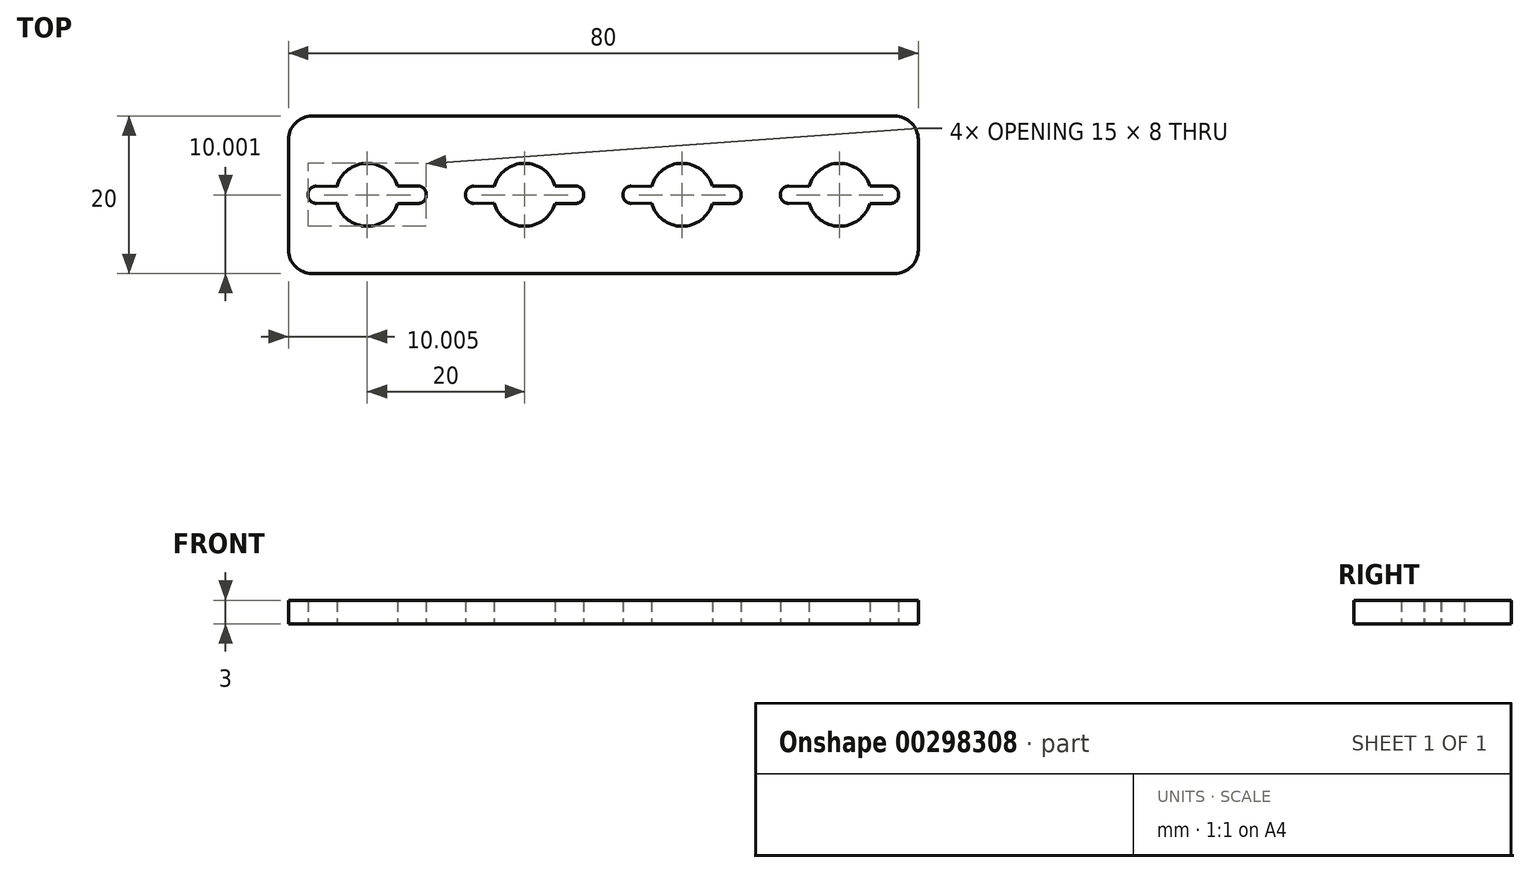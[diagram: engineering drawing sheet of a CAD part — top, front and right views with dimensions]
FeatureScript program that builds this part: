
annotation { "Feature Type Name" : "Feature", "Feature Type Description" : "" }
export const myFeature = defineFeature(function(context is Context, id is Id, definition is map)
    precondition{}
    {
        {
            var Q0;
            Q0=qCreatedBy(makeId("Top.planeOp"),FACE);
            var sketch = newSketch(context, id + "F0", { "sketchPlane" : qUnion([Q0])});
            skLineSegment(sketch, "E0.bottom", {"start": v(-30.97, -3.38) * mm, "end": v(43.03, -3.38) * mm});
            skLineSegment(sketch, "E0.top", {"start": v(-30.97, -23.38) * mm, "end": v(43.03, -23.38) * mm});
            skLineSegment(sketch, "E0.left", {"start": v(-33.97, -6.38) * mm, "end": v(-33.97, -20.38) * mm});
            skLineSegment(sketch, "E0.right", {"start": v(46.03, -6.38) * mm, "end": v(46.03, -20.38) * mm});
            skPoint(sketch, "E1.visualSharp", {"position": v(-33.97, -23.38) * mm});
            skArc(sketch, "E1.filletArc", {"start": v(-33.97, -20.38) * mm, "mid": v(-33.09, -22.5) * mm, "end": v(-30.97, -23.38) * mm});
            skPoint(sketch, "E2.visualSharp", {"position": v(-33.97, -3.38) * mm});
            skArc(sketch, "E2.filletArc", {"start": v(-30.97, -3.38) * mm, "mid": v(-33.09, -4.26) * mm, "end": v(-33.97, -6.38) * mm});
            skPoint(sketch, "E3.visualSharp", {"position": v(46.03, -3.38) * mm});
            skArc(sketch, "E3.filletArc", {"start": v(46.03, -6.38) * mm, "mid": v(45.16, -4.26) * mm, "end": v(43.03, -3.38) * mm});
            skPoint(sketch, "E4.visualSharp", {"position": v(46.03, -23.38) * mm});
            skArc(sketch, "E4.filletArc", {"start": v(43.03, -23.38) * mm, "mid": v(45.16, -22.5) * mm, "end": v(46.03, -20.38) * mm});
            skArc(sketch, "E5", {"start": v(-20.12, -12.28) * mm, "mid": v(-23.99, -9.38) * mm, "end": v(-27.82, -12.32) * mm});
            skLineSegment(sketch, "E6", {"start": v(-20.12, -12.28) * mm, "end": v(-17.47, -12.28) * mm});
            skLineSegment(sketch, "E7", {"start": v(-16.47, -13.28) * mm, "end": v(-16.47, -13.48) * mm});
            skLineSegment(sketch, "E8", {"start": v(-27.82, -12.32) * mm, "end": v(-30.45, -12.29) * mm});
            skLineSegment(sketch, "E9.MirrorCS", {"start": v(-20.12, -14.48) * mm, "end": v(-17.47, -14.48) * mm});
            skArc(sketch, "E10.MirrorCS", {"start": v(-20.12, -14.48) * mm, "mid": v(-23.99, -17.38) * mm, "end": v(-27.82, -14.44) * mm});
            skLineSegment(sketch, "E11.MirrorCS", {"start": v(-27.82, -14.44) * mm, "end": v(-30.45, -14.47) * mm});
            skLineSegment(sketch, "E12", {"start": v(-31.47, -13.29) * mm, "end": v(-31.47, -13.47) * mm});
            skPoint(sketch, "E13.visualSharp", {"position": v(-16.47, -12.28) * mm});
            skArc(sketch, "E13.filletArc", {"start": v(-16.47, -13.28) * mm, "mid": v(-16.76, -12.57) * mm, "end": v(-17.47, -12.28) * mm});
            skPoint(sketch, "E14.visualSharp", {"position": v(-16.47, -14.48) * mm});
            skArc(sketch, "E14.filletArc", {"start": v(-17.47, -14.48) * mm, "mid": v(-16.76, -14.19) * mm, "end": v(-16.47, -13.48) * mm});
            skPoint(sketch, "E15.visualSharp", {"position": v(-31.47, -12.28) * mm});
            skArc(sketch, "E15.filletArc", {"start": v(-30.45, -12.29) * mm, "mid": v(-31.17, -12.58) * mm, "end": v(-31.47, -13.29) * mm});
            skPoint(sketch, "E16.visualSharp", {"position": v(-31.47, -14.48) * mm});
            skArc(sketch, "E16.filletArc", {"start": v(-31.47, -13.47) * mm, "mid": v(-31.17, -14.18) * mm, "end": v(-30.45, -14.47) * mm});
            skLineSegment(sketch, "E17.1.0.0", {"start": v(-7.82, -12.32) * mm, "end": v(-10.45, -12.29) * mm});
            skPoint(sketch, "E17.1.0.1", {"position": v(3.53, -12.28) * mm});
            skLineSegment(sketch, "E17.1.0.2", {"start": v(-0.12, -12.28) * mm, "end": v(2.53, -12.28) * mm});
            skLineSegment(sketch, "E17.1.0.3", {"start": v(-0.12, -14.48) * mm, "end": v(2.53, -14.48) * mm});
            skPoint(sketch, "E17.1.0.4", {"position": v(3.53, -14.48) * mm});
            skArc(sketch, "E17.1.0.5", {"start": v(-0.12, -12.28) * mm, "mid": v(-3.99, -9.38) * mm, "end": v(-7.82, -12.32) * mm});
            skPoint(sketch, "E17.1.0.6", {"position": v(-11.47, -12.28) * mm});
            skPoint(sketch, "E17.1.0.7", {"position": v(-11.47, -14.48) * mm});
            skLineSegment(sketch, "E17.1.0.8", {"start": v(-7.82, -14.44) * mm, "end": v(-10.45, -14.47) * mm});
            skArc(sketch, "E17.1.0.9", {"start": v(-0.12, -14.48) * mm, "mid": v(-3.99, -17.38) * mm, "end": v(-7.82, -14.44) * mm});
            skArc(sketch, "E17.1.0.10", {"start": v(3.53, -13.28) * mm, "mid": v(3.24, -12.57) * mm, "end": v(2.53, -12.28) * mm});
            skArc(sketch, "E17.1.0.11", {"start": v(-10.45, -12.29) * mm, "mid": v(-11.17, -12.58) * mm, "end": v(-11.47, -13.29) * mm});
            skArc(sketch, "E17.1.0.12", {"start": v(2.53, -14.48) * mm, "mid": v(3.24, -14.19) * mm, "end": v(3.53, -13.48) * mm});
            skArc(sketch, "E17.1.0.13", {"start": v(-11.47, -13.47) * mm, "mid": v(-11.17, -14.18) * mm, "end": v(-10.45, -14.47) * mm});
            skLineSegment(sketch, "E17.1.0.14", {"start": v(3.53, -13.28) * mm, "end": v(3.53, -13.48) * mm});
            skLineSegment(sketch, "E17.1.0.15", {"start": v(-11.47, -13.29) * mm, "end": v(-11.47, -13.47) * mm});
            skLineSegment(sketch, "E17.2.0.0", {"start": v(12.18, -12.32) * mm, "end": v(9.55, -12.29) * mm});
            skPoint(sketch, "E17.2.0.1", {"position": v(23.53, -12.28) * mm});
            skLineSegment(sketch, "E17.2.0.2", {"start": v(19.88, -12.28) * mm, "end": v(22.53, -12.28) * mm});
            skLineSegment(sketch, "E17.2.0.3", {"start": v(19.88, -14.48) * mm, "end": v(22.53, -14.48) * mm});
            skPoint(sketch, "E17.2.0.4", {"position": v(23.53, -14.48) * mm});
            skArc(sketch, "E17.2.0.5", {"start": v(19.88, -12.28) * mm, "mid": v(16.01, -9.38) * mm, "end": v(12.18, -12.32) * mm});
            skPoint(sketch, "E17.2.0.6", {"position": v(8.53, -12.28) * mm});
            skPoint(sketch, "E17.2.0.7", {"position": v(8.53, -14.48) * mm});
            skLineSegment(sketch, "E17.2.0.8", {"start": v(12.18, -14.44) * mm, "end": v(9.55, -14.47) * mm});
            skArc(sketch, "E17.2.0.9", {"start": v(19.88, -14.48) * mm, "mid": v(16.01, -17.38) * mm, "end": v(12.18, -14.44) * mm});
            skArc(sketch, "E17.2.0.10", {"start": v(23.53, -13.28) * mm, "mid": v(23.24, -12.57) * mm, "end": v(22.53, -12.28) * mm});
            skArc(sketch, "E17.2.0.11", {"start": v(9.55, -12.29) * mm, "mid": v(8.83, -12.58) * mm, "end": v(8.53, -13.29) * mm});
            skArc(sketch, "E17.2.0.12", {"start": v(22.53, -14.48) * mm, "mid": v(23.24, -14.19) * mm, "end": v(23.53, -13.48) * mm});
            skArc(sketch, "E17.2.0.13", {"start": v(8.53, -13.47) * mm, "mid": v(8.83, -14.18) * mm, "end": v(9.55, -14.47) * mm});
            skLineSegment(sketch, "E17.2.0.14", {"start": v(23.53, -13.28) * mm, "end": v(23.53, -13.48) * mm});
            skLineSegment(sketch, "E17.2.0.15", {"start": v(8.53, -13.29) * mm, "end": v(8.53, -13.47) * mm});
            skLineSegment(sketch, "E17.3.0.0", {"start": v(32.18, -12.32) * mm, "end": v(29.55, -12.29) * mm});
            skPoint(sketch, "E17.3.0.1", {"position": v(43.53, -12.28) * mm});
            skLineSegment(sketch, "E17.3.0.2", {"start": v(39.88, -12.28) * mm, "end": v(42.53, -12.28) * mm});
            skLineSegment(sketch, "E17.3.0.3", {"start": v(39.88, -14.48) * mm, "end": v(42.53, -14.48) * mm});
            skPoint(sketch, "E17.3.0.4", {"position": v(43.53, -14.48) * mm});
            skArc(sketch, "E17.3.0.5", {"start": v(39.88, -12.28) * mm, "mid": v(36.01, -9.38) * mm, "end": v(32.18, -12.32) * mm});
            skPoint(sketch, "E17.3.0.6", {"position": v(28.53, -12.28) * mm});
            skPoint(sketch, "E17.3.0.7", {"position": v(28.53, -14.48) * mm});
            skLineSegment(sketch, "E17.3.0.8", {"start": v(32.18, -14.44) * mm, "end": v(29.55, -14.47) * mm});
            skArc(sketch, "E17.3.0.9", {"start": v(39.88, -14.48) * mm, "mid": v(36.01, -17.38) * mm, "end": v(32.18, -14.44) * mm});
            skArc(sketch, "E17.3.0.10", {"start": v(43.53, -13.28) * mm, "mid": v(43.24, -12.57) * mm, "end": v(42.53, -12.28) * mm});
            skArc(sketch, "E17.3.0.11", {"start": v(29.55, -12.29) * mm, "mid": v(28.83, -12.58) * mm, "end": v(28.53, -13.29) * mm});
            skArc(sketch, "E17.3.0.12", {"start": v(42.53, -14.48) * mm, "mid": v(43.24, -14.19) * mm, "end": v(43.53, -13.48) * mm});
            skArc(sketch, "E17.3.0.13", {"start": v(28.53, -13.47) * mm, "mid": v(28.83, -14.18) * mm, "end": v(29.55, -14.47) * mm});
            skLineSegment(sketch, "E17.3.0.14", {"start": v(43.53, -13.28) * mm, "end": v(43.53, -13.48) * mm});
            skLineSegment(sketch, "E17.3.0.15", {"start": v(28.53, -13.29) * mm, "end": v(28.53, -13.47) * mm});
            skLineSegment(sketch, "E17.direction1", {"start": v(-31.47, -14.48) * mm, "end": v(-11.47, -14.48) * mm, "construction": true});
            skSolve(sketch);
        }
        {
            var Q0;
            Q0 = qSketchRegion(id + "F0", true);
            extrude(context, id + "F1", {"entities" : qUnion([Q0]), "depth" : 3 * mm});
        }
    });
